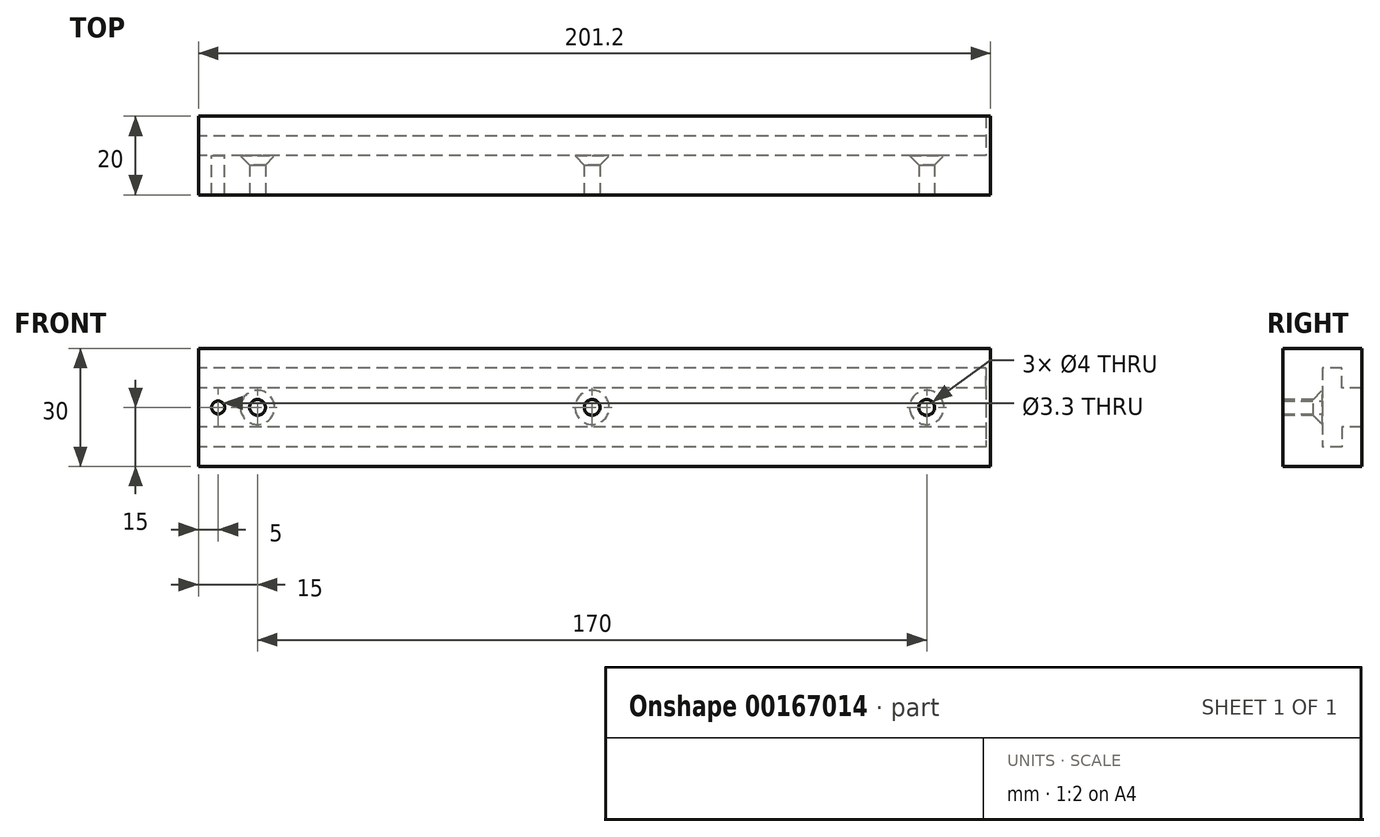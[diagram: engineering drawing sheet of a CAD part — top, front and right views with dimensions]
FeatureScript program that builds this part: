
annotation { "Feature Type Name" : "Feature", "Feature Type Description" : "" }
export const myFeature = defineFeature(function(context is Context, id is Id, definition is map)
    precondition{}
    {
        {
            var Q0;
            Q0=qCreatedBy(makeId("Right.planeOp"),FACE);
            var sketch = newSketch(context, id + "F0", { "sketchPlane" : qUnion([Q0])});
            skLineSegment(sketch, "E0", {"start": v(0, 0) * mm, "end": v(0, 30) * mm});
            skLineSegment(sketch, "E1", {"start": v(0, 30) * mm, "end": v(20, 30) * mm});
            skLineSegment(sketch, "E2", {"start": v(20, 30) * mm, "end": v(20, 25) * mm});
            skLineSegment(sketch, "E3", {"start": v(20, 25) * mm, "end": v(10, 25) * mm});
            skLineSegment(sketch, "E4", {"start": v(0, 15) * mm, "end": v(6.1, 15) * mm});
            skLineSegment(sketch, "E5", {"start": v(10, 25) * mm, "end": v(10, 15) * mm});
            skLineSegment(sketch, "E6.MirrorCS", {"start": v(10, 5) * mm, "end": v(10, 15) * mm});
            skLineSegment(sketch, "E7.MirrorCS", {"start": v(20, 5) * mm, "end": v(10, 5) * mm});
            skLineSegment(sketch, "E8.MirrorCS", {"start": v(20, 0) * mm, "end": v(20, 5) * mm});
            skLineSegment(sketch, "E9.MirrorCS", {"start": v(0, 0) * mm, "end": v(20, 0) * mm});
            skLineSegment(sketch, "E10", {"start": v(10, 15) * mm, "end": v(0, 15) * mm});
            skLineSegment(sketch, "E11", {"start": v(20, 25) * mm, "end": v(20, 20) * mm});
            skLineSegment(sketch, "E12", {"start": v(20, 20) * mm, "end": v(15, 20) * mm});
            skLineSegment(sketch, "E13", {"start": v(15, 20) * mm, "end": v(15, 25) * mm});
            skLineSegment(sketch, "E14.MirrorCS", {"start": v(20, 5) * mm, "end": v(20, 10) * mm});
            skLineSegment(sketch, "E15.MirrorCS", {"start": v(15, 10) * mm, "end": v(15, 5) * mm});
            skLineSegment(sketch, "E16.MirrorCS", {"start": v(20, 10) * mm, "end": v(15, 10) * mm});
            skSolve(sketch);
        }
        {
            var Q0;
            {var subQ3=sQuery(id+"F0.wireOp",EDGE,"E1");Q0=makeQuery(id+"F0.imprint","IMPRINT",FACE,{"disambiguationData":[TD([[makeQuery(id+"F0.imprint","IMPRINT",EDGE,{"derivedFrom":subQ3}),-1.0]])]});}
            var Q1;
            {var subQ0=sQuery(id+"F0.wireOp",EDGE,"E11");Q1=makeQuery(id+"F0.imprint","IMPRINT",FACE,{"disambiguationData":[TD([[makeQuery(id+"F0.imprint","IMPRINT",EDGE,{"derivedFrom":subQ0}),-1.0]])]});}
            var Q2;
            {var subQ0=sQuery(id+"F0.wireOp",EDGE,"E14.MirrorCS");Q2=makeQuery(id+"F0.imprint","IMPRINT",FACE,{"disambiguationData":[TD([[makeQuery(id+"F0.imprint","IMPRINT",EDGE,{"derivedFrom":subQ0}),1.0]])]});}
            var Q3;
            {var subQ1=sQuery(id+"F0.wireOp",EDGE,"E6.MirrorCS");Q3=makeQuery(id+"F0.imprint","IMPRINT",FACE,{"disambiguationData":[TD([[makeQuery(id+"F0.imprint","IMPRINT",EDGE,{"derivedFrom":subQ1}),1.0]])]});}
            extrude(context, id + "F1", {"entities" : qUnion([Q0, Q1, Q2, Q3]), "depth" : 200 * mm});
        }
        {
            var Q0;
            Q0=makeQuery(id+"F1.opExtrude","CAP_FACE",FACE,{"disambiguationData":[OSD([sQuery(id+"F0.wireOp",EDGE,"E0"),sQuery(id+"F0.wireOp",EDGE,"E1"),sQuery(id+"F0.wireOp",EDGE,"E2"),sQuery(id+"F0.wireOp",EDGE,"E3"),sQuery(id+"F0.wireOp",EDGE,"E5"),sQuery(id+"F0.wireOp",EDGE,"E6.MirrorCS"),sQuery(id+"F0.wireOp",EDGE,"E7.MirrorCS"),sQuery(id+"F0.wireOp",EDGE,"E8.MirrorCS"),sQuery(id+"F0.wireOp",EDGE,"E9.MirrorCS"),sQuery(id+"F0.wireOp",EDGE,"E11"),sQuery(id+"F0.wireOp",EDGE,"E12"),sQuery(id+"F0.wireOp",EDGE,"E13"),sQuery(id+"F0.wireOp",EDGE,"E14.MirrorCS"),sQuery(id+"F0.wireOp",EDGE,"E15.MirrorCS"),sQuery(id+"F0.wireOp",EDGE,"E16.MirrorCS")])],"isStart":false});
            var sketch = newSketch(context, id + "F2", { "sketchPlane" : qUnion([Q0])});
            skLineSegment(sketch, "E17", {"start": v(0, 30) * mm, "end": v(20, 30) * mm});
            skLineSegment(sketch, "E18", {"start": v(20, 30) * mm, "end": v(20, 0) * mm});
            skLineSegment(sketch, "E19", {"start": v(20, 0) * mm, "end": v(0, 0) * mm});
            skLineSegment(sketch, "E20", {"start": v(0, 0) * mm, "end": v(0, 30) * mm});
            skSolve(sketch);
        }
        {
            var Q0;
            {var subQ4=sQuery(id+"F2.wireOp",EDGE,"E17");Q0=makeQuery(id+"F2.imprint","IMPRINT",FACE,{"disambiguationData":[TD([[makeQuery(id+"F2.imprint","IMPRINT",EDGE,{"derivedFrom":subQ4}),-1.0]])]});}
            var Q1;
            Q1=makeQuery(id+"F2.imprint","IMPRINT",FACE,{"disambiguationData":[TD([[makeQuery(id+"F2.imprint","IMPRINT",EDGE,{"derivedFrom":makeQuery(id+"F1.opExtrude","CAP_EDGE",EDGE,{"disambiguationData":[OSD([sQuery(id+"F0.wireOp",EDGE,"E3")])],"isStart":false})}),1.0]])]});
            extrude(context, id + "F3", {"entities" : qUnion([Q0, Q1]), "operationType" : NewBodyOperationType.ADD, "depth" : 1.2 * mm});
        }
        {
            var Q0;
            Q0=makeQuery(id+"F1.opExtrude","SWEPT_FACE",FACE,{"disambiguationData":[OSD([sQuery(id+"F0.wireOp",EDGE,"E5"),sQuery(id+"F0.wireOp",EDGE,"E6.MirrorCS")])]});
            var sketch = newSketch(context, id + "F4", { "sketchPlane" : qUnion([Q0])});
            skLineSegment(sketch, "E21", {"start": v(0, 15) * mm, "end": v(-200, 15) * mm});
            skLineSegment(sketch, "E22", {"start": v(-200, 15) * mm, "end": v(-100, 15) * mm});
            skLineSegment(sketch, "E23", {"start": v(-100, 15) * mm, "end": v(-100, 17.07) * mm});
            skLineSegment(sketch, "E24", {"start": v(-200, 15) * mm, "end": v(-185, 15) * mm});
            skLineSegment(sketch, "E25", {"start": v(0, 15) * mm, "end": v(-15, 15) * mm});
            skLineSegment(sketch, "E26", {"start": v(0, 15) * mm, "end": v(-5, 15) * mm});
            skCircle(sketch, "E27", {"center": v(-5, 15) * mm, "radius": 1.65 * mm});
            skSolve(sketch);
        }
        {
            var Q0;
            Q0=sQuery(id+"F4.wireOp",VERTEX,"E25.end");
            var Q1;
            Q1=sQuery(id+"F4.wireOp",VERTEX,"E24.end");
            var Q2;
            Q2=sQuery(id+"F4.wireOp",VERTEX,"E23.start");
            var Q3;
            Q3=makeQuery(id+"F1.opExtrude","SWEPT_BODY",BODY,{"disambiguationData":[OSD([sQuery(id+"F0.wireOp",EDGE,"E0"),sQuery(id+"F0.wireOp",EDGE,"E1"),sQuery(id+"F0.wireOp",EDGE,"E2"),sQuery(id+"F0.wireOp",EDGE,"E3"),sQuery(id+"F0.wireOp",EDGE,"E5"),sQuery(id+"F0.wireOp",EDGE,"E6.MirrorCS"),sQuery(id+"F0.wireOp",EDGE,"E7.MirrorCS"),sQuery(id+"F0.wireOp",EDGE,"E8.MirrorCS"),sQuery(id+"F0.wireOp",EDGE,"E9.MirrorCS"),sQuery(id+"F0.wireOp",EDGE,"E11"),sQuery(id+"F0.wireOp",EDGE,"E12"),sQuery(id+"F0.wireOp",EDGE,"E13"),sQuery(id+"F0.wireOp",EDGE,"E14.MirrorCS"),sQuery(id+"F0.wireOp",EDGE,"E15.MirrorCS"),sQuery(id+"F0.wireOp",EDGE,"E16.MirrorCS")])]});
            hole(context, id + "F5", {"style" : HoleStyle.C_SINK, "endStyle" : HoleEndStyle.THROUGH, "holeDiameter" : 4 * mm, "cSinkDiameter" : 8.7 * mm, "cSinkAngle" : 90 * degree, "locations" : qUnion([Q0, Q1, Q2]), "scope" : qUnion([Q3]), "isTappedThrough" : true, "startStyle" : HoleStartStyle.PART});
        }
        {
            var Q0;
            Q0 = qSketchRegion(id + "F4", true);
            extrude(context, id + "F6", {"entities" : qUnion([Q0]), "operationType" : NewBodyOperationType.REMOVE, "oppositeDirection" : true, "depth" : 25 * mm});
        }
    });
